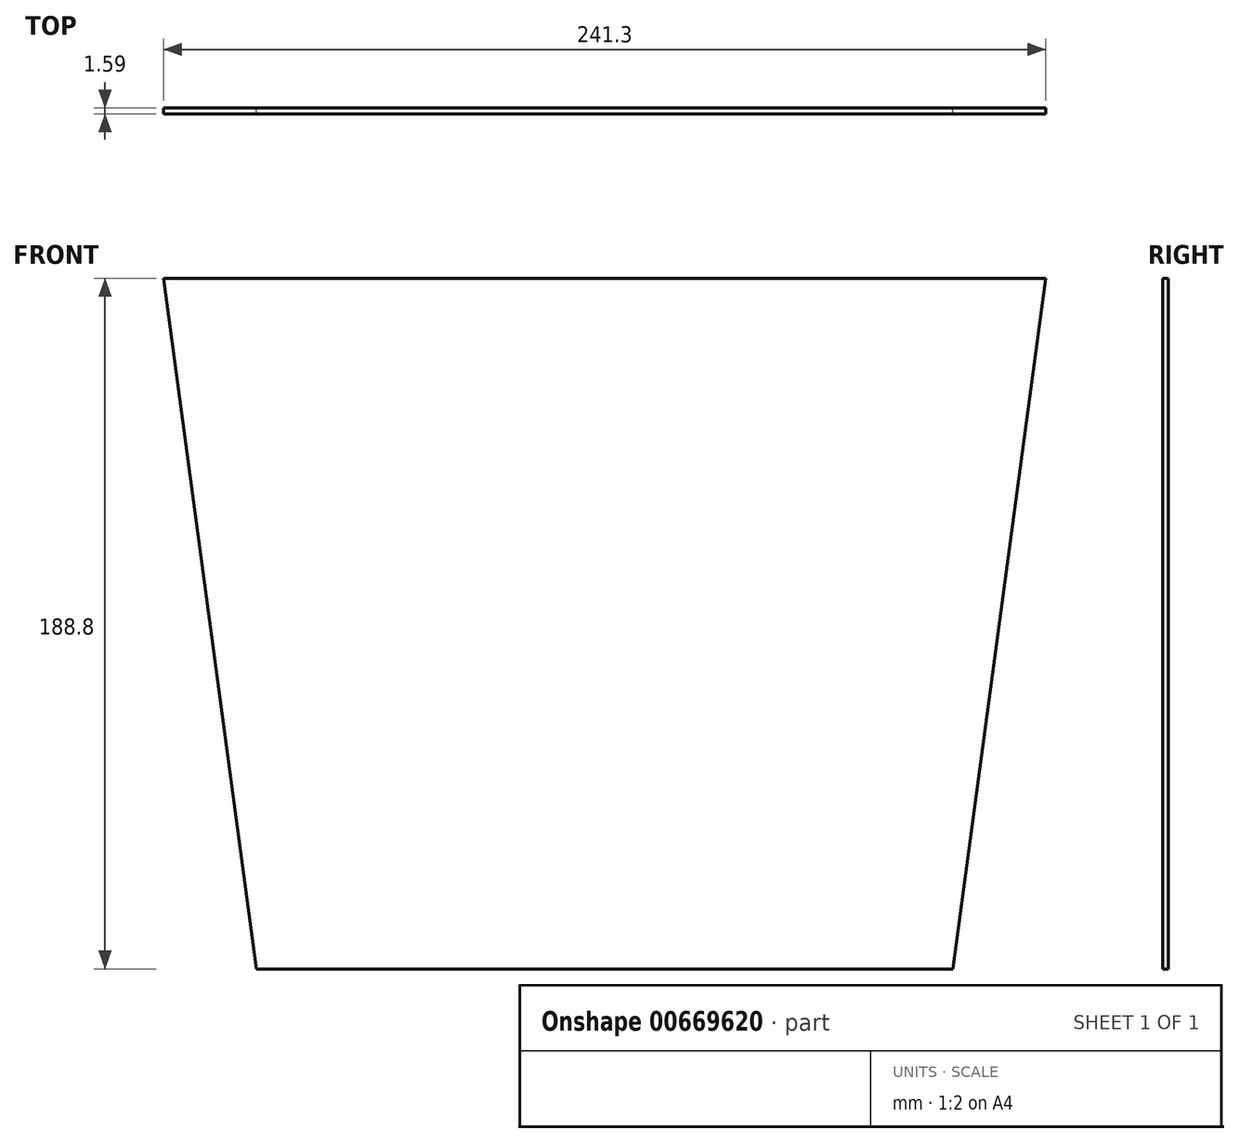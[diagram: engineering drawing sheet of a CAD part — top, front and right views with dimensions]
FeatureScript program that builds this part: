
annotation { "Feature Type Name" : "Feature", "Feature Type Description" : "" }
export const myFeature = defineFeature(function(context is Context, id is Id, definition is map)
    precondition{}
    {
        {
            var Q0;
            Q0=qCreatedBy(makeId("Front.planeOp"),FACE);
            var sketch = newSketch(context, id + "F0", { "sketchPlane" : qUnion([Q0])});
            skLineSegment(sketch, "E0", {"start": v(-146.18, 102.08) * mm, "end": v(95.12, 102.08) * mm});
            skLineSegment(sketch, "E1", {"start": v(95.12, 102.08) * mm, "end": v(69.72, -86.72) * mm});
            skLineSegment(sketch, "E2", {"start": v(69.72, -86.72) * mm, "end": v(-120.78, -86.72) * mm});
            skLineSegment(sketch, "E3", {"start": v(-120.78, -86.72) * mm, "end": v(-146.18, 102.08) * mm});
            skSolve(sketch);
        }
        {
            var Q0;
            Q0 = qSketchRegion(id + "F0", true);
            extrude(context, id + "F1", {"entities" : qUnion([Q0]), "depth" : 1.59 * mm, "offsetDistance" : 25.4 * mm});
        }
    });
